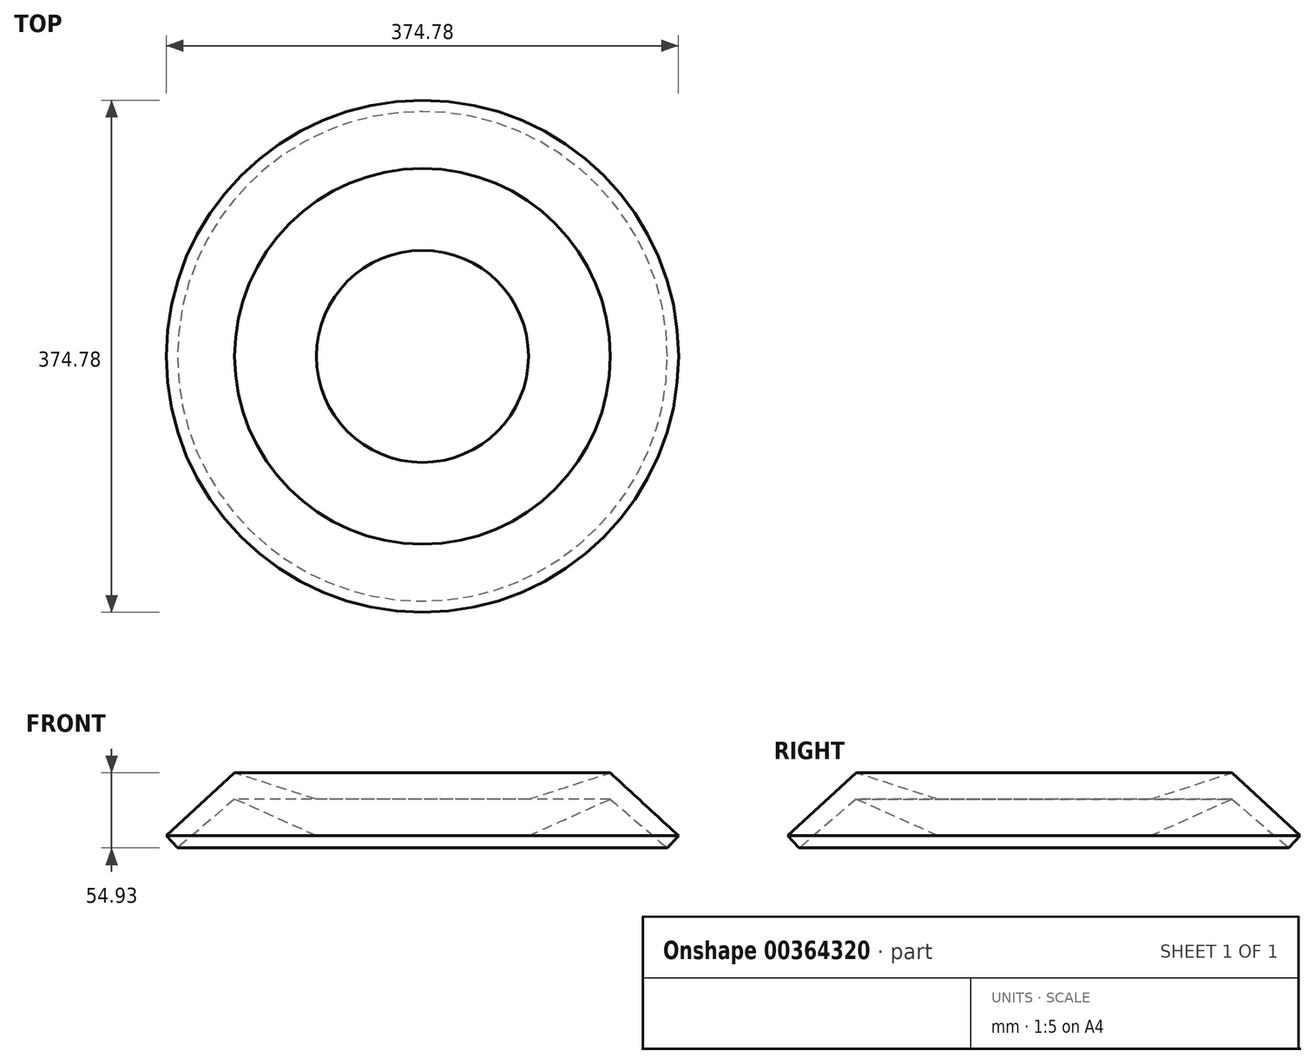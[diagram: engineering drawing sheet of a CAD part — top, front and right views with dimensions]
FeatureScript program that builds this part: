
annotation { "Feature Type Name" : "Feature", "Feature Type Description" : "" }
export const myFeature = defineFeature(function(context is Context, id is Id, definition is map)
    precondition{}
    {
        {
            var Q0;
            Q0=qCreatedBy(makeId("Front.planeOp"),FACE);
            var sketch = newSketch(context, id + "F0", { "sketchPlane" : qUnion([Q0])});
            skLineSegment(sketch, "E0.bottom", {"start": v(0, 0) * mm, "end": v(77.6, 0) * mm});
            skLineSegment(sketch, "E0.top", {"start": v(0, -26.77) * mm, "end": v(77.6, -26.77) * mm});
            skLineSegment(sketch, "E0.left", {"start": v(0, 0) * mm, "end": v(0, -26.77) * mm});
            skLineSegment(sketch, "E0.right", {"start": v(77.6, 0) * mm, "end": v(77.6, -26.77) * mm});
            skLineSegment(sketch, "E1", {"start": v(77.6, 0) * mm, "end": v(137.46, 19.25) * mm});
            skLineSegment(sketch, "E2", {"start": v(137.46, 19.25) * mm, "end": v(187.4, -26.77) * mm});
            skLineSegment(sketch, "E3", {"start": v(187.4, -26.77) * mm, "end": v(179.18, -35.68) * mm});
            skLineSegment(sketch, "E4", {"start": v(77.6, -26.77) * mm, "end": v(137.46, 0) * mm});
            skLineSegment(sketch, "E5", {"start": v(179.18, -35.68) * mm, "end": v(137.46, 0) * mm});
            skSolve(sketch);
        }
        {
            var Q0;
            Q0=makeQuery(id+"F0.imprint","IMPRINT",FACE,{"disambiguationData":[TD([[makeQuery(id+"F0.imprint","IMPRINT",EDGE,{"derivedFrom":sQuery(id+"F0.wireOp",EDGE,"E0.right")}),1.0]])]});
            var Q1;
            Q1=makeQuery(id+"F0.imprint","IMPRINT",FACE,{"disambiguationData":[TD([[makeQuery(id+"F0.imprint","IMPRINT",EDGE,{"derivedFrom":sQuery(id+"F0.wireOp",EDGE,"E0.bottom")}),-1.0]])]});
            var Q2;
            Q2=sQuery(id+"F0.wireOp",EDGE,"E0.left");
            revolve(context, id + "F1", {"entities" : qUnion([Q0, Q1]), "axis" : qUnion([Q2]), "revolveType" : RevolveType.FULL});
        }
    });
